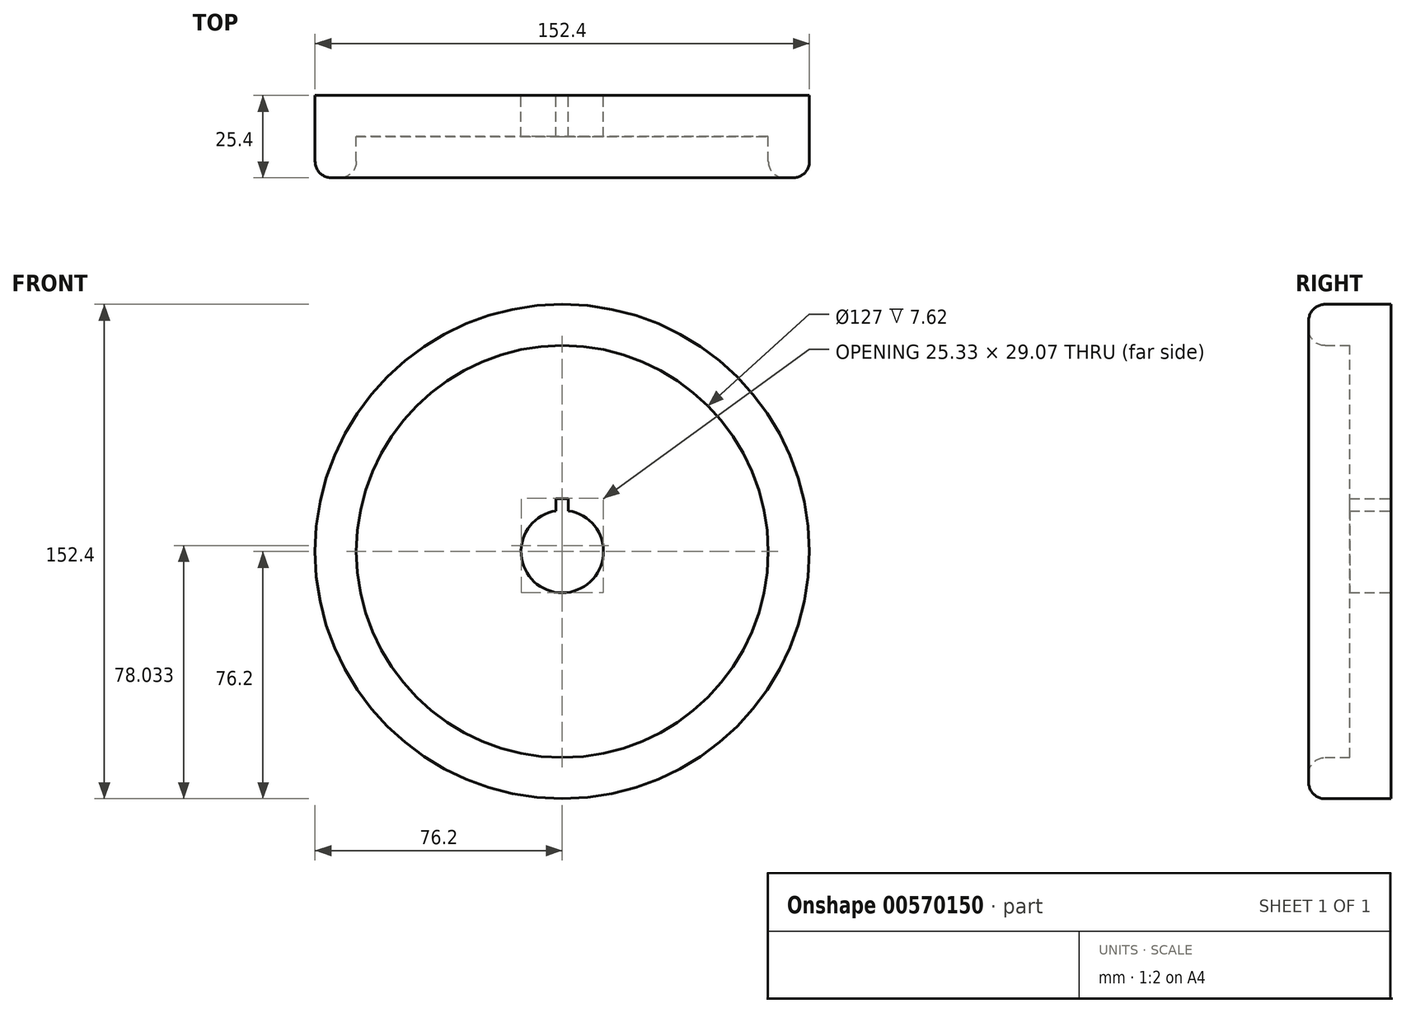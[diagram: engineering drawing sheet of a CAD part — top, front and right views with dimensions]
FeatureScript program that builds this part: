
annotation { "Feature Type Name" : "Feature", "Feature Type Description" : "" }
export const myFeature = defineFeature(function(context is Context, id is Id, definition is map)
    precondition{}
    {
        {
            var Q0;
            Q0=qCreatedBy(makeId("Front.planeOp"),FACE);
            var sketch = newSketch(context, id + "F0", { "sketchPlane" : qUnion([Q0])});
            skArc(sketch, "E0", {"start": v(-1.9, 12.56) * mm, "mid": v(0, -12.7) * mm, "end": v(1.9, 12.56) * mm});
            skCircle(sketch, "E1", {"center": v(0, 0) * mm, "radius": 63.5 * mm});
            skCircle(sketch, "E2", {"center": v(0, 0) * mm, "radius": 76.2 * mm});
            skLineSegment(sketch, "E3", {"start": v(-1.9, 12.56) * mm, "end": v(-1.9, 16.37) * mm});
            skLineSegment(sketch, "E4", {"start": v(-1.9, 16.37) * mm, "end": v(1.9, 16.37) * mm});
            skLineSegment(sketch, "E5", {"start": v(1.9, 16.37) * mm, "end": v(1.9, 12.56) * mm});
            skSolve(sketch);
        }
        {
            var Q0;
            Q0=makeQuery(id+"F0.imprint","IMPRINT",FACE,{"disambiguationData":[TD([[makeQuery(id+"F0.imprint","IMPRINT",EDGE,{"derivedFrom":sQuery(id+"F0.wireOp",EDGE,"E1")}),-1.0]])]});
            extrude(context, id + "F1", {"entities" : qUnion([Q0]), "depth" : 25.4 * mm, "offsetDistance" : 25.4 * mm});
        }
        {
            var Q0;
            Q0=makeQuery(id+"F0.imprint","IMPRINT",FACE,{"disambiguationData":[TD([[makeQuery(id+"F0.imprint","IMPRINT",EDGE,{"derivedFrom":sQuery(id+"F0.wireOp",EDGE,"E0")}),-1.0]])]});
            extrude(context, id + "F2", {"entities" : qUnion([Q0]), "operationType" : NewBodyOperationType.ADD, "depth" : 12.7 * mm, "offsetDistance" : 25.4 * mm});
        }
        {
            var Q0;
            Q0=makeQuery(id+"F1.opExtrude","CAP_EDGE",EDGE,{"disambiguationData":[OSD([sQuery(id+"F0.wireOp",EDGE,"E2")])],"isStart":false});
            var Q1;
            Q1=makeQuery(id+"F1.opExtrude","CAP_EDGE",EDGE,{"disambiguationData":[OSD([sQuery(id+"F0.wireOp",EDGE,"E1")])],"isStart":false});
            fillet(context, id + "F3", {"entities" : qUnion([Q0, Q1]), "radius" : 5.08 * mm, "tangentPropagation" : true, "allowEdgeOverflow" : false});
        }
    });
